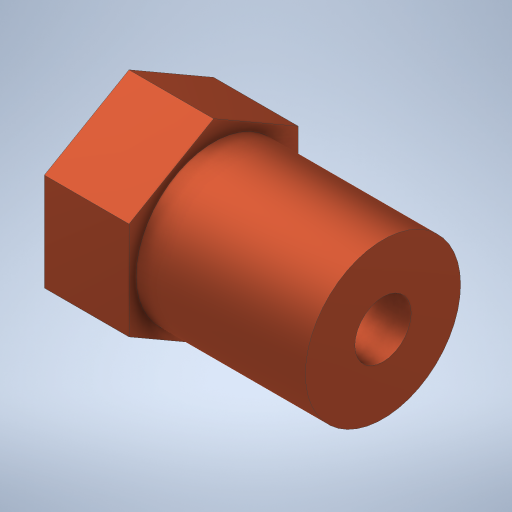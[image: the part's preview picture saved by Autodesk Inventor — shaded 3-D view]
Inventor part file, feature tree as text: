
AUTODESK INVENTOR PART (.ipt)
format: ipt  version: 2023 (Build 270158000, 158)  size: 244,224 bytes
history: native  units: mm
features: extrude x3, sketch x3
ambient origin geometry x8: Origin, YZ Plane, XZ Plane, XY Plane, X Axis, Y Axis, Z Axis, Center Point
bodies: Volumenkörper1 (feature_tree)
feature tree (6):
  extrude  "Extrusion1"  Depth=6.0mm TaperAngle=0.0deg
  extrude  "Extrusion2"  Depth=12.0mm TaperAngle=0.0deg
  extrude  "Extrusion3"  TaperAngle=0.0deg  [1 undecoded]
  sketch  "Skizze1"  dims[d0=12.0mm d1=6.0mm d2=0.0mm]
  sketch  "Skizze2"  dims[d3=11.0mm d4=12.0mm d5=0.0mm]
  sketch  "Skizze3"  dims[d6=4.0mm d7=0.0mm d8=0.0mm]
note: 1 required parameter value undecoded (feature->parameter linkage not recoverable at this tier; creation-order binding heuristic only, values carry confidence <= 0.55)
